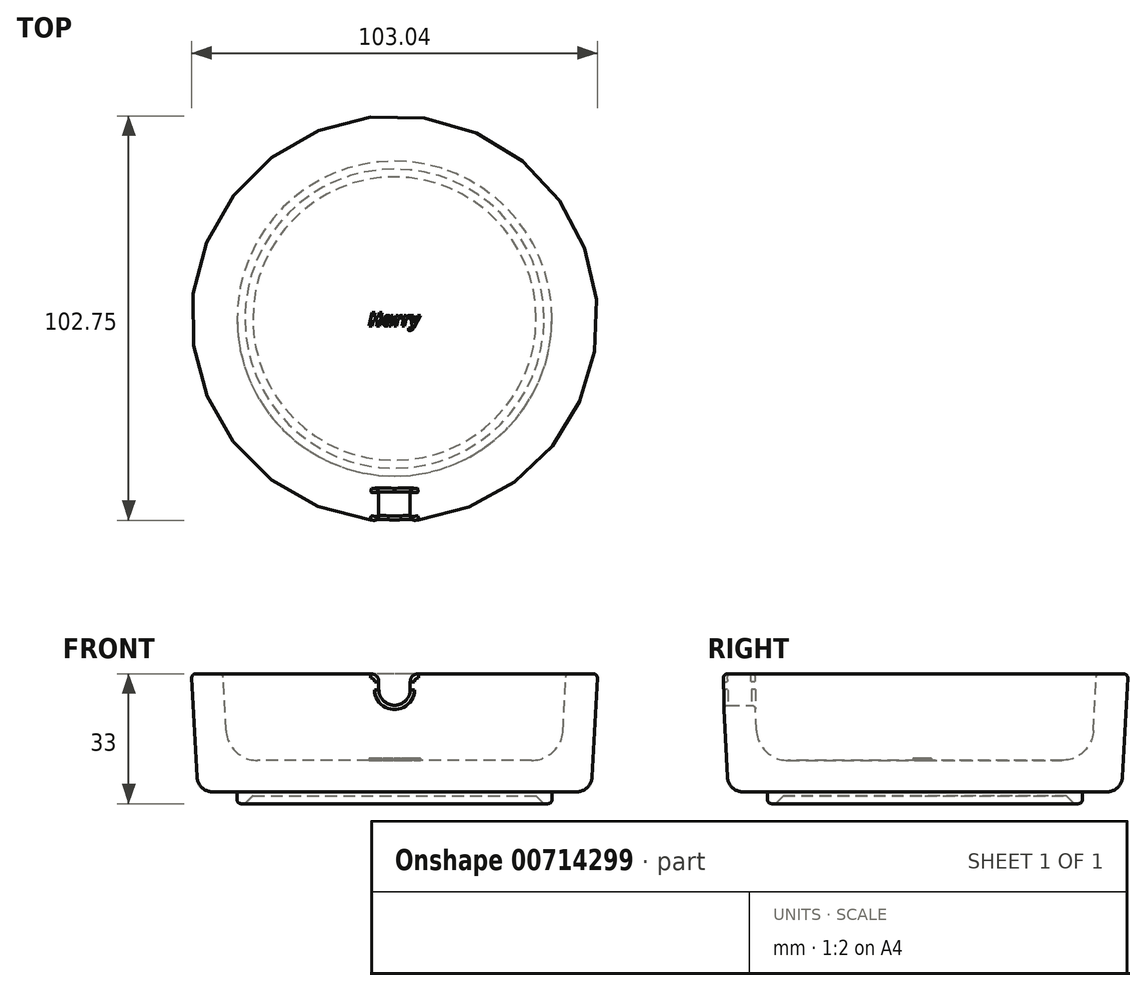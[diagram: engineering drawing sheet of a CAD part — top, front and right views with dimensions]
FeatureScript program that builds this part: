
annotation { "Feature Type Name" : "Feature", "Feature Type Description" : "" }
export const myFeature = defineFeature(function(context is Context, id is Id, definition is map)
    precondition{}
    {
        {
            var Q0;
            Q0=qCreatedBy(makeId("Top.planeOp"),FACE);
            var sketch = newSketch(context, id + "F0", { "sketchPlane" : qUnion([Q0])});
            skCircle(sketch, "E0", {"center": v(0, 0) * mm, "radius": 50 * mm});
            skSolve(sketch);
        }
        {
            var Q0;
            Q0=makeQuery(id+"F0.imprint","IMPRINT",FACE,{"disambiguationData":[TD([[makeQuery(id+"F0.imprint","IMPRINT",EDGE,{"derivedFrom":sQuery(id+"F0.wireOp",EDGE,"E0")}),1.0]])]});
            extrude(context, id + "F1", {"entities" : qUnion([Q0]), "depth" : 30 * mm, "offsetDistance" : 25.4 * mm, "hasDraft" : true, "draftAngle" : 3 * degree});
        }
        {
            var Q0;
            Q0=makeQuery(id+"F1.opExtrude","CAP_EDGE",EDGE,{"disambiguationData":[OSD([sQuery(id+"F0.wireOp",EDGE,"E0")])],"isStart":true});
            fillet(context, id + "F2", {"entities" : qUnion([Q0]), "radius" : 4 * mm, "tangentPropagation" : true, "allowEdgeOverflow" : false});
        }
        {
            var Q0;
            Q0=makeQuery(id+"F1.opExtrude","CAP_FACE",FACE,{"disambiguationData":[OSD([sQuery(id+"F0.wireOp",EDGE,"E0")])],"isStart":false});
            shell(context, id + "F3", {"entities" : qUnion([Q0]), "thickness" : 8 * mm});
        }
        {
            var Q0;
            Q0=makeQuery(id+"F1.opExtrude","CAP_FACE",FACE,{"disambiguationData":[OSD([sQuery(id+"F0.wireOp",EDGE,"E0")])],"isStart":true});
            var sketch = newSketch(context, id + "F4", { "sketchPlane" : qUnion([Q0])});
            skCircle(sketch, "E1", {"center": v(0, 0) * mm, "radius": 40 * mm});
            skSolve(sketch);
        }
        {
            var Q0;
            Q0 = qSketchRegion(id + "F4", true);
            extrude(context, id + "F5", {"entities" : qUnion([Q0]), "operationType" : NewBodyOperationType.ADD, "depth" : 3 * mm, "offsetDistance" : 25.4 * mm});
        }
        {
            var Q0;
            {var subQ0=sQuery(id+"F0.wireOp",EDGE,"E0");var subQ1=makeQuery(id+"F1.opExtrude","CAP_EDGE",EDGE,{"disambiguationData":[OSD([subQ0])],"isStart":true});Q0=makeQuery(id+"F3.opShell","OFFSET_EDGE",EDGE,{"disambiguationData":[OSD([subQ0]),TDD([makeQuery(id+"F2.opFillet","BLEND_EDGE",EDGE,{"blendedFrom":[subQ1,makeQuery(id+"F1.opExtrude","CAP_FACE",FACE,{"disambiguationData":[OSD([subQ0])],"isStart":true})],"blendedInto":[makeQuery(id+"F1.opExtrude","CAP_FACE",FACE,{"disambiguationData":[OSD([subQ0])],"isStart":true})]}),makeQuery(id+"F2.opFillet","BLEND_EDGE",EDGE,{"blendedFrom":[subQ1,makeQuery(id+"F1.opExtrude","SWEPT_FACE",FACE,{"disambiguationData":[OSD([subQ0])]})],"blendedInto":[makeQuery(id+"F1.opExtrude","SWEPT_FACE",FACE,{"disambiguationData":[OSD([subQ0])]})]})])]});}
            fillet(context, id + "F6", {"entities" : qUnion([Q0]), "radius" : 8 * mm, "tangentPropagation" : true, "allowEdgeOverflow" : false});
        }
        {
            var Q0;
            Q0=qCreatedBy(makeId("Front.planeOp"),FACE);
            var sketch = newSketch(context, id + "F7", { "sketchPlane" : qUnion([Q0])});
            skArc(sketch, "E2", {"start": v(-4, 26) * mm, "mid": v(0, 22) * mm, "end": v(4, 26) * mm});
            skLineSegment(sketch, "E3", {"start": v(-4, 26) * mm, "end": v(-4, 109.97) * mm});
            skLineSegment(sketch, "E4", {"start": v(-4, 109.97) * mm, "end": v(4, 109.97) * mm});
            skLineSegment(sketch, "E5", {"start": v(4, 26) * mm, "end": v(4, 109.97) * mm});
            skPoint(sketch, "E6.orphan", {"position": v(18.14, 109.97) * mm});
            skSolve(sketch);
        }
        {
            var Q0;
            Q0 = qSketchRegion(id + "F7", true);
            extrude(context, id + "F8", {"entities" : qUnion([Q0]), "operationType" : NewBodyOperationType.REMOVE, "endBound" : BoundingType.THROUGH_ALL, "depth" : 25.4 * mm, "offsetDistance" : 25.4 * mm});
        }
        {
            var Q0;
            Q0=makeQuery(id+"F5.opExtrude","CAP_EDGE",EDGE,{"disambiguationData":[OSD([sQuery(id+"F4.wireOp",EDGE,"E1")])],"isStart":false});
            fillet(context, id + "F9", {"entities" : qUnion([Q0]), "radius" : 1 * mm, "tangentPropagation" : true, "allowEdgeOverflow" : false});
        }
        {
            var Q0;
            {var subQ0=sQuery(id+"F7.wireOp",EDGE,"E3");var subQ1=sQuery(id+"F0.wireOp",EDGE,"E0");var subQ3=makeQuery(id+"F8.boolean.opBoolean","COPY",FACE,{"derivedFrom":makeQuery(id+"F8.opExtrude","SWEPT_FACE",FACE,{"disambiguationData":[OSD([subQ0])]})});Q0=makeQuery(id+"FjvzY9mzfnETUdn_1.3.F8.boolean.opBoolean","INTERSECT",EDGE,{"derivedFrom":[makeQuery(id+"FjvzY9mzfnETUdn_1.2.F8.boolean.opBoolean","SPLIT",FACE,{"disambiguationData":[TD([subQ3])],"derivedFrom":makeQuery(id+"FjvzY9mzfnETUdn_1.1.F8.boolean.opBoolean","SPLIT",FACE,{"disambiguationData":[TD([subQ3])],"derivedFrom":makeQuery(id+"F1.opExtrude","CAP_FACE",FACE,{"disambiguationData":[OSD([subQ1])],"isStart":false})})}),makeQuery(id+"FjvzY9mzfnETUdn_1.3.F8.opExtrude","SWEPT_FACE",FACE,{"disambiguationData":[OSD([subQ0])]})]});}
            var Q1;
            {var subQ0=sQuery(id+"F7.wireOp",EDGE,"E5");var subQ1=sQuery(id+"F0.wireOp",EDGE,"E0");var subQ3=makeQuery(id+"F8.boolean.opBoolean","COPY",FACE,{"derivedFrom":makeQuery(id+"F8.opExtrude","SWEPT_FACE",FACE,{"disambiguationData":[OSD([sQuery(id+"F7.wireOp",EDGE,"E3")])]})});Q1=makeQuery(id+"FjvzY9mzfnETUdn_1.3.F8.boolean.opBoolean","INTERSECT",EDGE,{"derivedFrom":[makeQuery(id+"FjvzY9mzfnETUdn_1.2.F8.boolean.opBoolean","SPLIT",FACE,{"disambiguationData":[TD([subQ3])],"derivedFrom":makeQuery(id+"FjvzY9mzfnETUdn_1.1.F8.boolean.opBoolean","SPLIT",FACE,{"disambiguationData":[TD([subQ3])],"derivedFrom":makeQuery(id+"F1.opExtrude","CAP_FACE",FACE,{"disambiguationData":[OSD([subQ1])],"isStart":false})})}),makeQuery(id+"FjvzY9mzfnETUdn_1.3.F8.opExtrude","SWEPT_FACE",FACE,{"disambiguationData":[OSD([subQ0])]})]});}
            var Q2;
            {var subQ0=sQuery(id+"F7.wireOp",EDGE,"E5");var subQ1=sQuery(id+"F0.wireOp",EDGE,"E0");Q2=makeQuery(id+"FjvzY9mzfnETUdn_1.2.F8.boolean.opBoolean","INTERSECT",EDGE,{"derivedFrom":[makeQuery(id+"FjvzY9mzfnETUdn_1.1.F8.boolean.opBoolean","SPLIT",FACE,{"disambiguationData":[TD([makeQuery(id+"F8.boolean.opBoolean","COPY",FACE,{"derivedFrom":makeQuery(id+"F8.opExtrude","SWEPT_FACE",FACE,{"disambiguationData":[OSD([sQuery(id+"F7.wireOp",EDGE,"E3")])]})})])],"derivedFrom":makeQuery(id+"F1.opExtrude","CAP_FACE",FACE,{"disambiguationData":[OSD([subQ1])],"isStart":false})}),makeQuery(id+"FjvzY9mzfnETUdn_1.2.F8.opExtrude","SWEPT_FACE",FACE,{"disambiguationData":[OSD([subQ0])]})]});}
            var Q3;
            {var subQ0=sQuery(id+"F7.wireOp",EDGE,"E3");var subQ1=sQuery(id+"F0.wireOp",EDGE,"E0");Q3=makeQuery(id+"FjvzY9mzfnETUdn_1.2.F8.boolean.opBoolean","INTERSECT",EDGE,{"derivedFrom":[makeQuery(id+"FjvzY9mzfnETUdn_1.1.F8.boolean.opBoolean","SPLIT",FACE,{"disambiguationData":[TD([makeQuery(id+"F8.boolean.opBoolean","COPY",FACE,{"derivedFrom":makeQuery(id+"F8.opExtrude","SWEPT_FACE",FACE,{"disambiguationData":[OSD([subQ0])]})})])],"derivedFrom":makeQuery(id+"F1.opExtrude","CAP_FACE",FACE,{"disambiguationData":[OSD([subQ1])],"isStart":false})}),makeQuery(id+"FjvzY9mzfnETUdn_1.2.F8.opExtrude","SWEPT_FACE",FACE,{"disambiguationData":[OSD([subQ0])]})]});}
            var Q4;
            Q4=makeQuery(id+"FjvzY9mzfnETUdn_1.1.F8.boolean.opBoolean","INTERSECT",EDGE,{"derivedFrom":[makeQuery(id+"F1.opExtrude","CAP_FACE",FACE,{"disambiguationData":[OSD([sQuery(id+"F0.wireOp",EDGE,"E0")])],"isStart":false}),makeQuery(id+"FjvzY9mzfnETUdn_1.1.F8.opExtrude","SWEPT_FACE",FACE,{"disambiguationData":[OSD([sQuery(id+"F7.wireOp",EDGE,"E5")])]})]});
            var Q5;
            Q5=makeQuery(id+"FjvzY9mzfnETUdn_1.1.F8.boolean.opBoolean","INTERSECT",EDGE,{"derivedFrom":[makeQuery(id+"F1.opExtrude","CAP_FACE",FACE,{"disambiguationData":[OSD([sQuery(id+"F0.wireOp",EDGE,"E0")])],"isStart":false}),makeQuery(id+"FjvzY9mzfnETUdn_1.1.F8.opExtrude","SWEPT_FACE",FACE,{"disambiguationData":[OSD([sQuery(id+"F7.wireOp",EDGE,"E3")])]})]});
            var Q6;
            Q6=makeQuery(id+"F8.boolean.opBoolean","INTERSECT",EDGE,{"derivedFrom":[makeQuery(id+"F1.opExtrude","CAP_FACE",FACE,{"disambiguationData":[OSD([sQuery(id+"F0.wireOp",EDGE,"E0")])],"isStart":false}),makeQuery(id+"F8.opExtrude","SWEPT_FACE",FACE,{"disambiguationData":[OSD([sQuery(id+"F7.wireOp",EDGE,"E5")])]})]});
            var Q7;
            Q7=makeQuery(id+"F8.boolean.opBoolean","INTERSECT",EDGE,{"derivedFrom":[makeQuery(id+"F1.opExtrude","CAP_FACE",FACE,{"disambiguationData":[OSD([sQuery(id+"F0.wireOp",EDGE,"E0")])],"isStart":false}),makeQuery(id+"F8.opExtrude","SWEPT_FACE",FACE,{"disambiguationData":[OSD([sQuery(id+"F7.wireOp",EDGE,"E3")])]})]});
            fillet(context, id + "F10", {"entities" : qUnion([Q0, Q1, Q2, Q3, Q4, Q5, Q6, Q7]), "radius" : 2 * mm, "tangentPropagation" : true, "allowEdgeOverflow" : false});
        }
        {
            var Q0;
            {var subQ0=sQuery(id+"F0.wireOp",EDGE,"E0");var subQ2=makeQuery(id+"F8.boolean.opBoolean","COPY",FACE,{"derivedFrom":makeQuery(id+"F8.opExtrude","SWEPT_FACE",FACE,{"disambiguationData":[OSD([sQuery(id+"F7.wireOp",EDGE,"E3")])]})});Q0=makeQuery(id+"FjvzY9mzfnETUdn_1.3.F8.boolean.opBoolean","SPLIT",EDGE,{"disambiguationData":[TD([subQ2])],"derivedFrom":makeQuery(id+"FjvzY9mzfnETUdn_1.2.F8.boolean.opBoolean","SPLIT",EDGE,{"disambiguationData":[TD([subQ2])],"derivedFrom":makeQuery(id+"FjvzY9mzfnETUdn_1.1.F8.boolean.opBoolean","SPLIT",EDGE,{"disambiguationData":[TD([subQ2])],"derivedFrom":makeQuery(id+"F1.opExtrude","CAP_EDGE",EDGE,{"disambiguationData":[OSD([subQ0])],"isStart":false})})})});}
            fillet(context, id + "F11", {"entities" : qUnion([Q0]), "radius" : 1 * mm, "tangentPropagation" : true, "allowEdgeOverflow" : false});
        }
        {
            var Q0;
            {var subQ0=sQuery(id+"F0.wireOp",EDGE,"E0");var subQ2=sQuery(id+"F7.wireOp",EDGE,"E3");var subQ4=sQuery(id+"F7.wireOp",EDGE,"E5");var subQ5=makeQuery(id+"FjvzY9mzfnETUdn_1.2.F8.opExtrude","SWEPT_FACE",FACE,{"disambiguationData":[OSD([subQ4])]});var subQ6=makeQuery(id+"F8.boolean.opBoolean","COPY",FACE,{"derivedFrom":makeQuery(id+"F8.opExtrude","SWEPT_FACE",FACE,{"disambiguationData":[OSD([subQ2])]})});Q0=makeQuery(id+"FjvzY9mzfnETUdn_1.3.F8.boolean.opBoolean","SPLIT",EDGE,{"disambiguationData":[TD([makeQuery(id+"FjvzY9mzfnETUdn_1.2.F8.boolean.opBoolean","COPY",FACE,{"derivedFrom":subQ5})])],"derivedFrom":makeQuery(id+"FjvzY9mzfnETUdn_1.2.F8.boolean.opBoolean","SPLIT",EDGE,{"disambiguationData":[TD([subQ6])],"derivedFrom":makeQuery(id+"FjvzY9mzfnETUdn_1.1.F8.boolean.opBoolean","SPLIT",EDGE,{"disambiguationData":[TD([subQ6])],"derivedFrom":makeQuery(id+"F3.opShell","OFFSET_EDGE",EDGE,{"disambiguationData":[OSD([subQ0]),TDD([makeQuery(id+"F1.opExtrude","CAP_EDGE",EDGE,{"disambiguationData":[OSD([subQ0])],"isStart":false})])]})})})});}
            fillet(context, id + "F12", {"entities" : qUnion([Q0]), "radius" : 1 * mm, "tangentPropagation" : true, "allowEdgeOverflow" : false});
        }
        {
            var Q0;
            Q0=qCreatedBy(makeId("Top.planeOp"),FACE);
            var sketch = newSketch(context, id + "F13", { "sketchPlane" : qUnion([Q0])});
            skText(sketch, "E7", { "text": "Harry", "fontName": "OpenSans-BoldItalic.ttf"});
            const initialGuessF13  = {"E7": [-0.00655, -0.00186, 1, 0, 0.0035]};
            skSetInitialGuess(sketch, initialGuessF13);
            skSolve(sketch);
        }
        {
            var Q0;
            Q0 = qSketchRegion(id + "F13", true);
            var Q1;
            Q1 = qBodyType(qCreatedBy(id + "F13" ,EDGE), BodyType.WIRE);
            extrude(context, id + "F14", {"entities" : qUnion([Q0]), "operationType" : NewBodyOperationType.ADD, "surfaceEntities" : qUnion([Q1]), "depth" : 8.5 * mm, "offsetDistance" : 25 * mm});
        }
        {
            var Q0;
            Q0=qCreatedBy(makeId("Front.planeOp"),FACE);
            var sketch = newSketch(context, id + "F15", { "sketchPlane" : qUnion([Q0])});
            skLineSegment(sketch, "E8", {"start": v(-38, -3) * mm, "end": v(-36, -1) * mm});
            skLineSegment(sketch, "E9", {"start": v(-36, -1) * mm, "end": v(0, -1) * mm});
            skLineSegment(sketch, "E10", {"start": v(0, -1) * mm, "end": v(0, -3) * mm});
            skLineSegment(sketch, "E11", {"start": v(0, -3) * mm, "end": v(-38, -3) * mm});
            skSolve(sketch);
        }
        {
            var Q0;
            Q0 = qSketchRegion(id + "F15", true);
            var Q1;
            Q1=sQuery(id+"F15.wireOp",EDGE,"E10");
            revolve(context, id + "F16", {"operationType" : NewBodyOperationType.REMOVE, "surfaceOperationType" : NewSurfaceOperationType.NEW, "entities" : qUnion([Q0]), "axis" : qUnion([Q1]), "revolveType" : RevolveType.FULL, "oppositeDirection" : true});
        }
    });
